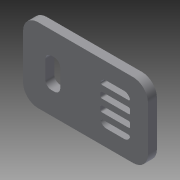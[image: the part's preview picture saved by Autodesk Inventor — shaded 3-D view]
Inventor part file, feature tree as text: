
AUTODESK INVENTOR PART (.ipt)
format: ipt  version: 2015 (Build 190159000, 159)  size: 148,992 bytes
history: native  units: mm
features: extrude x1, sketch x1
ambient origin geometry x8: Origin, YZ Plane, XZ Plane, XY Plane, X Axis, Y Axis, Z Axis, Center Point
bodies: Body1 (feature_tree)
feature tree (2):
  extrude  "Extrusion2"  Depth=25.0mm
  sketch  "Sketch1"  dims[d0=42.0mm d2=25.0mm d3=5.0mm d4=5.0mm d5=5.0mm d6=3.0mm d8=5.5mm d9=10.0mm d10=2.0mm d15=2.0mm d16=2.0mm d17=2.0mm d18=2.0mm d19=2.0mm d21=2.0mm d23=0.5mm d30=2.0mm d31=6.0mm d32=16.0mm d37=5.0mm d41=5.0mm d42=42.0mm d43=7.5mm d44=10.0mm d45=7.5mm d46=2.0mm d47=3.0mm d48=0.0mm d49=5.0mm]
